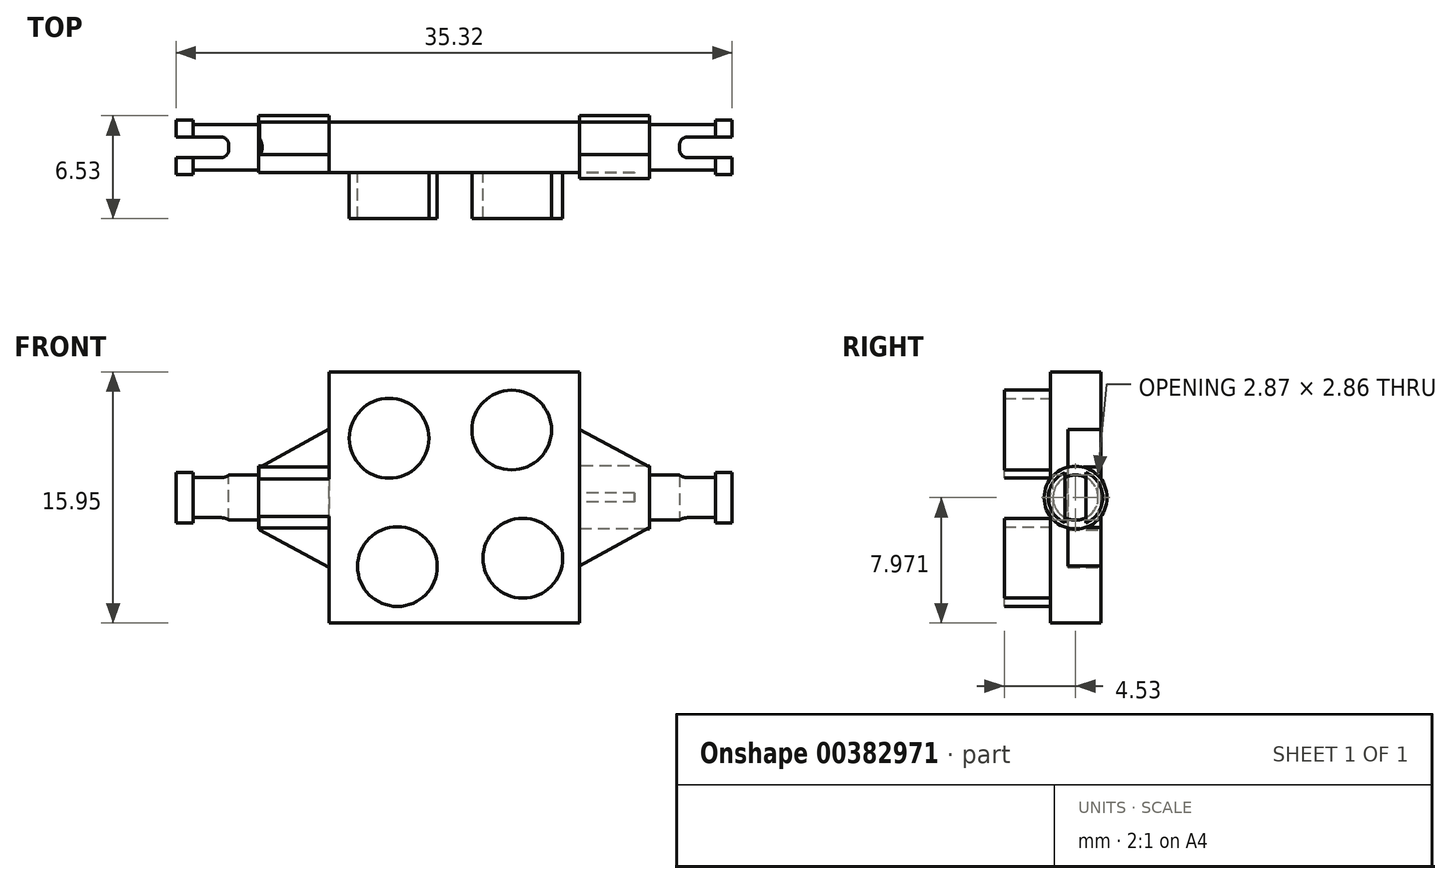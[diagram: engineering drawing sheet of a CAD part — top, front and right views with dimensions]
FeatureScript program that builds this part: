
annotation { "Feature Type Name" : "Feature", "Feature Type Description" : "" }
export const myFeature = defineFeature(function(context is Context, id is Id, definition is map)
    precondition{}
    {
        {
            var Q0;
            Q0=qCreatedBy(makeId("Front.planeOp"),FACE);
            var sketch = newSketch(context, id + "F0", { "sketchPlane" : qUnion([Q0])});
            skLineSegment(sketch, "E0.bottom", {"start": v(0, 0) * mm, "end": v(15.9, 0) * mm});
            skLineSegment(sketch, "E0.top", {"start": v(0, 15.95) * mm, "end": v(15.9, 15.95) * mm});
            skLineSegment(sketch, "E0.left", {"start": v(0, 0) * mm, "end": v(0, 15.95) * mm});
            skLineSegment(sketch, "E0.right", {"start": v(15.9, 0) * mm, "end": v(15.9, 15.95) * mm});
            skSolve(sketch);
        }
        {
            var Q0;
            Q0=makeQuery(id+"F0.imprint","IMPRINT",FACE,{"disambiguationData":[TD([[makeQuery(id+"F0.imprint","IMPRINT",EDGE,{"derivedFrom":sQuery(id+"F0.wireOp",EDGE,"E0.bottom")}),1.0]])]});
            extrude(context, id + "F1", {"entities" : qUnion([Q0]), "depth" : 3.2 * mm});
        }
        {
            var Q0;
            Q0=makeQuery(id+"F1.opExtrude","CAP_FACE",FACE,{"disambiguationData":[OSD([sQuery(id+"F0.wireOp",EDGE,"E0.bottom"),sQuery(id+"F0.wireOp",EDGE,"E0.top"),sQuery(id+"F0.wireOp",EDGE,"E0.left"),sQuery(id+"F0.wireOp",EDGE,"E0.right")])],"isStart":false});
            var sketch = newSketch(context, id + "F2", { "sketchPlane" : qUnion([Q0])});
            skCircle(sketch, "E1", {"center": v(3.82, 11.75) * mm, "radius": 2.53 * mm});
            skCircle(sketch, "E2", {"center": v(11.6, 12.27) * mm, "radius": 2.53 * mm});
            skCircle(sketch, "E3", {"center": v(4.34, 3.6) * mm, "radius": 2.53 * mm});
            skCircle(sketch, "E4", {"center": v(12.31, 4.13) * mm, "radius": 2.53 * mm});
            skSolve(sketch);
        }
        {
            var Q0;
            Q0=makeQuery(id+"F2.imprint","IMPRINT",FACE,{"disambiguationData":[TD([[makeQuery(id+"F2.imprint","IMPRINT",EDGE,{"derivedFrom":sQuery(id+"F2.wireOp",EDGE,"E1")}),1.0]])]});
            var Q1;
            Q1=makeQuery(id+"F2.imprint","IMPRINT",FACE,{"disambiguationData":[TD([[makeQuery(id+"F2.imprint","IMPRINT",EDGE,{"derivedFrom":sQuery(id+"F2.wireOp",EDGE,"E2")}),1.0]])]});
            var Q2;
            Q2=makeQuery(id+"F2.imprint","IMPRINT",FACE,{"disambiguationData":[TD([[makeQuery(id+"F2.imprint","IMPRINT",EDGE,{"derivedFrom":sQuery(id+"F2.wireOp",EDGE,"E3")}),1.0]])]});
            var Q3;
            Q3=makeQuery(id+"F2.imprint","IMPRINT",FACE,{"disambiguationData":[TD([[makeQuery(id+"F2.imprint","IMPRINT",EDGE,{"derivedFrom":sQuery(id+"F2.wireOp",EDGE,"E4")}),1.0]])]});
            extrude(context, id + "F3", {"entities" : qUnion([Q0, Q1, Q2, Q3]), "operationType" : NewBodyOperationType.ADD, "depth" : 2.93 * mm});
        }
        {
            var Q0;
            Q0=makeQuery(id+"F1.opExtrude","SWEPT_FACE",FACE,{"disambiguationData":[OSD([sQuery(id+"F0.wireOp",EDGE,"E0.left")])]});
            var sketch = newSketch(context, id + "F4", { "sketchPlane" : qUnion([Q0])});
            skCircle(sketch, "E5", {"center": v(1.6, 7.97) * mm, "radius": 2 * mm});
            skPoint(sketch, "E5.centerSnap0", {"position": v(3.2, 7.97) * mm});
            skPoint(sketch, "E5.centerSnap1", {"position": v(1.6, 15.95) * mm});
            skSolve(sketch);
        }
        {
            var Q0;
            {var subQ0=sQuery(id+"F4.wireOp",EDGE,"E5");var subQ1=sQuery(id+"F0.wireOp",EDGE,"E0.left");var subQ2=makeQuery(id+"F1.opExtrude","CAP_EDGE",EDGE,{"disambiguationData":[OSD([subQ1])],"isStart":true});var subQ3=makeQuery(id+"F4.imprint","INTERSECT",VERTEX,{"disambiguationData":[OD(0.0)],"derivedFrom":[subQ2,subQ0]});Q0=makeQuery(id+"F4.imprint","IMPRINT",FACE,{"disambiguationData":[TD([[makeQuery(id+"F4.imprint","IMPRINT",EDGE,{"disambiguationData":[TD([[subQ3,1.0]])],"derivedFrom":subQ0}),1.0]])]});}
            var Q1;
            {var subQ0=sQuery(id+"F4.wireOp",EDGE,"E5");var subQ1=makeQuery(id+"F1.opExtrude","CAP_EDGE",EDGE,{"disambiguationData":[OSD([sQuery(id+"F0.wireOp",EDGE,"E0.left")])],"isStart":false});var subQ2=makeQuery(id+"F4.imprint","INTERSECT",VERTEX,{"disambiguationData":[OD(0.0)],"derivedFrom":[subQ1,subQ0]});Q1=makeQuery(id+"F4.imprint","IMPRINT",FACE,{"disambiguationData":[TD([[makeQuery(id+"F4.imprint","IMPRINT",EDGE,{"disambiguationData":[TD([[subQ2,1.0]])],"derivedFrom":subQ0}),1.0]])]});}
            var Q2;
            {var subQ0=sQuery(id+"F4.wireOp",EDGE,"E5");var subQ1=makeQuery(id+"F1.opExtrude","CAP_EDGE",EDGE,{"disambiguationData":[OSD([sQuery(id+"F0.wireOp",EDGE,"E0.left")])],"isStart":true});var subQ2=makeQuery(id+"F4.imprint","INTERSECT",VERTEX,{"disambiguationData":[OD(0.0)],"derivedFrom":[subQ1,subQ0]});Q2=makeQuery(id+"F4.imprint","IMPRINT",FACE,{"disambiguationData":[TD([[makeQuery(id+"F4.imprint","IMPRINT",EDGE,{"disambiguationData":[TD([[subQ2,-1.0]])],"derivedFrom":subQ0}),1.0]])]});}
            extrude(context, id + "F5", {"entities" : qUnion([Q0, Q1, Q2]), "operationType" : NewBodyOperationType.ADD, "depth" : 4.47 * mm});
        }
        {
            var Q0;
            Q0=makeQuery(id+"F5.opExtrude","CAP_FACE",FACE,{"disambiguationData":[OSD([sQuery(id+"F4.wireOp",EDGE,"E5")])],"isStart":false});
            var sketch = newSketch(context, id + "F6", { "sketchPlane" : qUnion([Q0])});
            skCircle(sketch, "E6", {"center": v(1.6, 7.97) * mm, "radius": 1.44 * mm});
            skSolve(sketch);
        }
        {
            var Q0;
            Q0=makeQuery(id+"F6.imprint","IMPRINT",FACE,{"disambiguationData":[TD([[makeQuery(id+"F6.imprint","IMPRINT",EDGE,{"derivedFrom":sQuery(id+"F6.wireOp",EDGE,"E6")}),1.0]])]});
            extrude(context, id + "F7", {"entities" : qUnion([Q0]), "operationType" : NewBodyOperationType.ADD, "depth" : 5.24 * mm});
        }
        {
            var Q0;
            Q0=makeQuery(id+"F7.opExtrude","CAP_FACE",FACE,{"disambiguationData":[OSD([sQuery(id+"F6.wireOp",EDGE,"E6")])],"isStart":false});
            var sketch = newSketch(context, id + "F8", { "sketchPlane" : qUnion([Q0])});
            skCircle(sketch, "E7", {"center": v(1.6, 7.97) * mm, "radius": 1.73 * mm});
            skSolve(sketch);
        }
        {
            var Q0;
            Q0=qSketchRegion(id+"F8",true);
            extrude(context, id + "F9", {"entities" : qUnion([Q0]), "operationType" : NewBodyOperationType.ADD, "oppositeDirection" : true, "depth" : 1.07 * mm});
        }
        {
            var Q0;
            Q0=makeQuery(id+"F9.boolean.opBoolean","MERGE",FACE,{"derivedFrom":[makeQuery(id+"F7.opExtrude","CAP_FACE",FACE,{"disambiguationData":[OSD([sQuery(id+"F6.wireOp",EDGE,"E6")])],"isStart":false}),makeQuery(id+"F9.opExtrude","CAP_FACE",FACE,{"disambiguationData":[OSD([sQuery(id+"F8.wireOp",EDGE,"E7")])],"isStart":true})]});
            var sketch = newSketch(context, id + "F10", { "sketchPlane" : qUnion([Q0])});
            skLineSegment(sketch, "E8.left", {"start": v(2.26, 6.38) * mm, "end": v(2.26, 9.57) * mm});
            skLineSegment(sketch, "E8.right", {"start": v(0.94, 6.38) * mm, "end": v(0.94, 9.57) * mm});
            skPoint(sketch, "E8.middle", {"position": v(1.6, 7.97) * mm});
            skArc(sketch, "E9", {"start": v(2.26, 9.57) * mm, "mid": v(1.6, 9.74) * mm, "end": v(0.94, 9.57) * mm});
            skArc(sketch, "E10", {"start": v(0.94, 6.38) * mm, "mid": v(1.6, 6.19) * mm, "end": v(2.26, 6.38) * mm});
            skSolve(sketch);
        }
        {
            var Q0;
            Q0=qSketchRegion(id+"F10",true);
            extrude(context, id + "F11", {"entities" : qUnion([Q0]), "operationType" : NewBodyOperationType.REMOVE, "oppositeDirection" : true, "depth" : 3.34 * mm});
        }
        {
            var Q0;
            Q0=makeQuery(id+"F11.boolean.opBoolean","COPY",EDGE,{"derivedFrom":makeQuery(id+"F11.opExtrude","CAP_EDGE",EDGE,{"disambiguationData":[OSD([sQuery(id+"F10.wireOp",EDGE,"E8.left")])],"isStart":false})});
            var Q1;
            Q1=makeQuery(id+"F11.boolean.opBoolean","COPY",EDGE,{"derivedFrom":makeQuery(id+"F11.opExtrude","CAP_EDGE",EDGE,{"disambiguationData":[OSD([sQuery(id+"F10.wireOp",EDGE,"E8.right")])],"isStart":false})});
            fillet(context, id + "F12", {"entities" : qUnion([Q0, Q1]), "radius" : .5 * mm, "tangentPropagation" : true, "allowEdgeOverflow" : false});
        }
        {
            var Q0;
            Q0=qCreatedBy(makeId("Front.planeOp"),FACE);
            var sketch = newSketch(context, id + "F13", { "sketchPlane" : qUnion([Q0])});
            skLineSegment(sketch, "E11", {"start": v(0, 3.53) * mm, "end": v(-4.4, 5.9) * mm});
            skLineSegment(sketch, "E12", {"start": v(-4.4, 5.9) * mm, "end": v(-4.4, 9.9) * mm});
            skLineSegment(sketch, "E13", {"start": v(-4.4, 9.9) * mm, "end": v(0, 12.33) * mm});
            skLineSegment(sketch, "E14", {"start": v(0, 12.33) * mm, "end": v(0, 3.53) * mm});
            skSolve(sketch);
        }
        {
            var Q0;
            Q0=makeQuery(id+"F13.imprint","IMPRINT",FACE,{"disambiguationData":[TD([[makeQuery(id+"F13.imprint","IMPRINT",EDGE,{"derivedFrom":sQuery(id+"F13.wireOp",EDGE,"E11")}),-1.0]])]});
            extrude(context, id + "F14", {"entities" : qUnion([Q0]), "operationType" : NewBodyOperationType.ADD, "depth" : 2.08 * mm});
        }
        {
            var Q0;
            Q0=makeQuery(id+"F1.opExtrude","SWEPT_FACE",FACE,{"disambiguationData":[OSD([sQuery(id+"F0.wireOp",EDGE,"E0.right")])]});
            var sketch = newSketch(context, id + "F15", { "sketchPlane" : qUnion([Q0])});
            skCircle(sketch, "E15", {"center": v(-1.6, 7.97) * mm, "radius": 1.63 * mm});
            skPoint(sketch, "E15.centerSnap0", {"position": v(-3.2, 7.97) * mm});
            skPoint(sketch, "E15.centerSnap1", {"position": v(-1.6, 0) * mm});
            skSolve(sketch);
        }
        {
            var Q0;
            {var subQ0=sQuery(id+"F15.wireOp",EDGE,"E15");var subQ1=makeQuery(id+"F1.opExtrude","CAP_EDGE",EDGE,{"disambiguationData":[OSD([sQuery(id+"F0.wireOp",EDGE,"E0.right")])],"isStart":false});var subQ2=makeQuery(id+"F15.imprint","INTERSECT",VERTEX,{"disambiguationData":[OD(0.0)],"derivedFrom":[subQ1,subQ0]});Q0=makeQuery(id+"F15.imprint","IMPRINT",FACE,{"disambiguationData":[TD([[makeQuery(id+"F15.imprint","IMPRINT",EDGE,{"disambiguationData":[TD([[subQ2,-1.0]])],"derivedFrom":subQ0}),1.0]])]});}
            var Q1;
            {var subQ0=sQuery(id+"F15.wireOp",EDGE,"E15");var subQ1=makeQuery(id+"F1.opExtrude","CAP_EDGE",EDGE,{"disambiguationData":[OSD([sQuery(id+"F0.wireOp",EDGE,"E0.right")])],"isStart":true});var subQ2=makeQuery(id+"F15.imprint","INTERSECT",VERTEX,{"disambiguationData":[OD(0.0)],"derivedFrom":[subQ1,subQ0]});Q1=makeQuery(id+"F15.imprint","IMPRINT",FACE,{"disambiguationData":[TD([[makeQuery(id+"F15.imprint","IMPRINT",EDGE,{"disambiguationData":[TD([[subQ2,1.0]])],"derivedFrom":subQ0}),1.0]])]});}
            extrude(context, id + "F16", {"entities" : qUnion([Q0, Q1]), "depth" : 3.52 * mm});
        }
        {
            var Q0;
            Q0=makeQuery(id+"F1.opExtrude","SWEPT_FACE",FACE,{"disambiguationData":[OSD([sQuery(id+"F0.wireOp",EDGE,"E0.right")])]});
            var sketch = newSketch(context, id + "F17", { "sketchPlane" : qUnion([Q0])});
            skCircle(sketch, "E16", {"center": v(-1.6, 7.97) * mm, "radius": 2 * mm});
            skPoint(sketch, "E16.centerSnap0", {"position": v(-3.2, 7.97) * mm});
            skPoint(sketch, "E16.centerSnap1", {"position": v(-1.6, 0) * mm});
            skSolve(sketch);
        }
        {
            var Q0;
            Q0=qSketchRegion(id+"F17",true);
            var Q1;
            {var subQ0=sQuery(id+"F17.wireOp",EDGE,"E16");var subQ1=sQuery(id+"F0.wireOp",EDGE,"E0.right");var subQ2=makeQuery(id+"F1.opExtrude","CAP_EDGE",EDGE,{"disambiguationData":[OSD([subQ1])],"isStart":false});var subQ3=makeQuery(id+"F17.imprint","INTERSECT",VERTEX,{"disambiguationData":[OD(0.0)],"derivedFrom":[subQ2,subQ0]});Q1=makeQuery(id+"F17.imprint","IMPRINT",FACE,{"disambiguationData":[TD([[makeQuery(id+"F17.imprint","IMPRINT",EDGE,{"disambiguationData":[TD([[subQ3,1.0]])],"derivedFrom":subQ0}),1.0]])]});}
            extrude(context, id + "F18", {"entities" : qUnion([Q0, Q1]), "depth" : 4.47 * mm});
        }
        {
            var Q0;
            Q0=makeQuery(id+"F18.opExtrude","CAP_FACE",FACE,{"disambiguationData":[OSD([sQuery(id+"F17.wireOp",EDGE,"E16")])],"isStart":false});
            var sketch = newSketch(context, id + "F19", { "sketchPlane" : qUnion([Q0])});
            skCircle(sketch, "E17", {"center": v(-1.6, 7.97) * mm, "radius": 1.44 * mm});
            skSolve(sketch);
        }
        {
            var Q0;
            Q0=qSketchRegion(id+"F19",true);
            var Q1;
            Q1=makeQuery(id+"F19.imprint","IMPRINT",FACE,{"disambiguationData":[TD([[makeQuery(id+"F19.imprint","IMPRINT",EDGE,{"derivedFrom":sQuery(id+"F19.wireOp",EDGE,"E17")}),1.0]])]});
            extrude(context, id + "F20", {"entities" : qUnion([Q0, Q1]), "operationType" : NewBodyOperationType.ADD, "depth" : 5.24 * mm});
        }
        {
            var Q0;
            Q0=makeQuery(id+"F20.opExtrude","CAP_FACE",FACE,{"disambiguationData":[OSD([sQuery(id+"F19.wireOp",EDGE,"E17")])],"isStart":false});
            var sketch = newSketch(context, id + "F21", { "sketchPlane" : qUnion([Q0])});
            skCircle(sketch, "E18", {"center": v(-1.6, 7.97) * mm, "radius": 1.73 * mm});
            skSolve(sketch);
        }
        {
            var Q0;
            Q0=qSketchRegion(id+"F21",true);
            extrude(context, id + "F22", {"entities" : qUnion([Q0]), "operationType" : NewBodyOperationType.ADD, "oppositeDirection" : true, "depth" : 1.07 * mm});
        }
        {
            var Q0;
            Q0=makeQuery(id+"F22.boolean.opBoolean","MERGE",FACE,{"derivedFrom":[makeQuery(id+"F20.opExtrude","CAP_FACE",FACE,{"disambiguationData":[OSD([sQuery(id+"F19.wireOp",EDGE,"E17")])],"isStart":false}),makeQuery(id+"F22.opExtrude","CAP_FACE",FACE,{"disambiguationData":[OSD([sQuery(id+"F21.wireOp",EDGE,"E18")])],"isStart":true})]});
            var sketch = newSketch(context, id + "F23", { "sketchPlane" : qUnion([Q0])});
            skLineSegment(sketch, "E19.left", {"start": v(-2.26, 9.57) * mm, "end": v(-2.26, 6.38) * mm});
            skLineSegment(sketch, "E19.right", {"start": v(-0.94, 9.57) * mm, "end": v(-0.94, 6.38) * mm});
            skPoint(sketch, "E19.middle", {"position": v(-1.6, 7.97) * mm});
            skArc(sketch, "E20", {"start": v(-2.26, 6.38) * mm, "mid": v(-1.6, 6.18) * mm, "end": v(-0.94, 6.38) * mm});
            skArc(sketch, "E21", {"start": v(-0.94, 9.57) * mm, "mid": v(-1.6, 9.75) * mm, "end": v(-2.26, 9.57) * mm});
            skSolve(sketch);
        }
        {
            var Q0;
            {var subQ0=sQuery(id+"F23.wireOp",EDGE,"E19.left");Q0=makeQuery(id+"F23.imprint","IMPRINT",FACE,{"disambiguationData":[TD([[makeQuery(id+"F23.imprint","IMPRINT",EDGE,{"derivedFrom":subQ0}),1.0]])]});}
            extrude(context, id + "F24", {"entities" : qUnion([Q0]), "operationType" : NewBodyOperationType.REMOVE, "oppositeDirection" : true, "depth" : 3.34 * mm});
        }
        {
            var Q0;
            Q0=makeQuery(id+"F24.boolean.opBoolean","COPY",EDGE,{"derivedFrom":makeQuery(id+"F24.opExtrude","CAP_EDGE",EDGE,{"disambiguationData":[OSD([sQuery(id+"F23.wireOp",EDGE,"E19.left")])],"isStart":false})});
            var Q1;
            Q1=makeQuery(id+"F24.boolean.opBoolean","COPY",EDGE,{"derivedFrom":makeQuery(id+"F24.opExtrude","CAP_EDGE",EDGE,{"disambiguationData":[OSD([sQuery(id+"F23.wireOp",EDGE,"E19.right")])],"isStart":false})});
            fillet(context, id + "F25", {"entities" : qUnion([Q0, Q1]), "radius" : .5 * mm, "tangentPropagation" : true, "allowEdgeOverflow" : false});
        }
        {
            var Q0;
            Q0=makeQuery(id+"F14.boolean.opBoolean","MERGE",FACE,{"derivedFrom":[makeQuery(id+"F1.opExtrude","CAP_FACE",FACE,{"disambiguationData":[OSD([sQuery(id+"F0.wireOp",EDGE,"E0.bottom"),sQuery(id+"F0.wireOp",EDGE,"E0.top"),sQuery(id+"F0.wireOp",EDGE,"E0.left"),sQuery(id+"F0.wireOp",EDGE,"E0.right")])],"isStart":true}),makeQuery(id+"F14.opExtrude","CAP_FACE",FACE,{"disambiguationData":[OSD([sQuery(id+"F13.wireOp",EDGE,"E11"),sQuery(id+"F13.wireOp",EDGE,"E12"),sQuery(id+"F13.wireOp",EDGE,"E13"),sQuery(id+"F13.wireOp",EDGE,"E14")])],"isStart":true})]});
            var sketch = newSketch(context, id + "F26", { "sketchPlane" : qUnion([Q0])});
            skPoint(sketch, "E22", {"position": v(-15.9, 12.3) * mm});
            skPoint(sketch, "E23", {"position": v(-15.9, 3.64) * mm});
            skLineSegment(sketch, "E24", {"start": v(-15.9, 12.3) * mm, "end": v(-20.35, 9.91) * mm});
            skLineSegment(sketch, "E25", {"start": v(-20.35, 9.91) * mm, "end": v(-20.35, 6.1) * mm});
            skLineSegment(sketch, "E26", {"start": v(-20.35, 6.1) * mm, "end": v(-15.9, 3.64) * mm});
            skLineSegment(sketch, "E27", {"start": v(-15.9, 12.3) * mm, "end": v(-15.9, 3.64) * mm});
            skSolve(sketch);
        }
        {
            var Q0;
            Q0=qSketchRegion(id+"F26",true);
            extrude(context, id + "F27", {"entities" : qUnion([Q0]), "oppositeDirection" : true, "depth" : 2.08 * mm});
        }
    });
